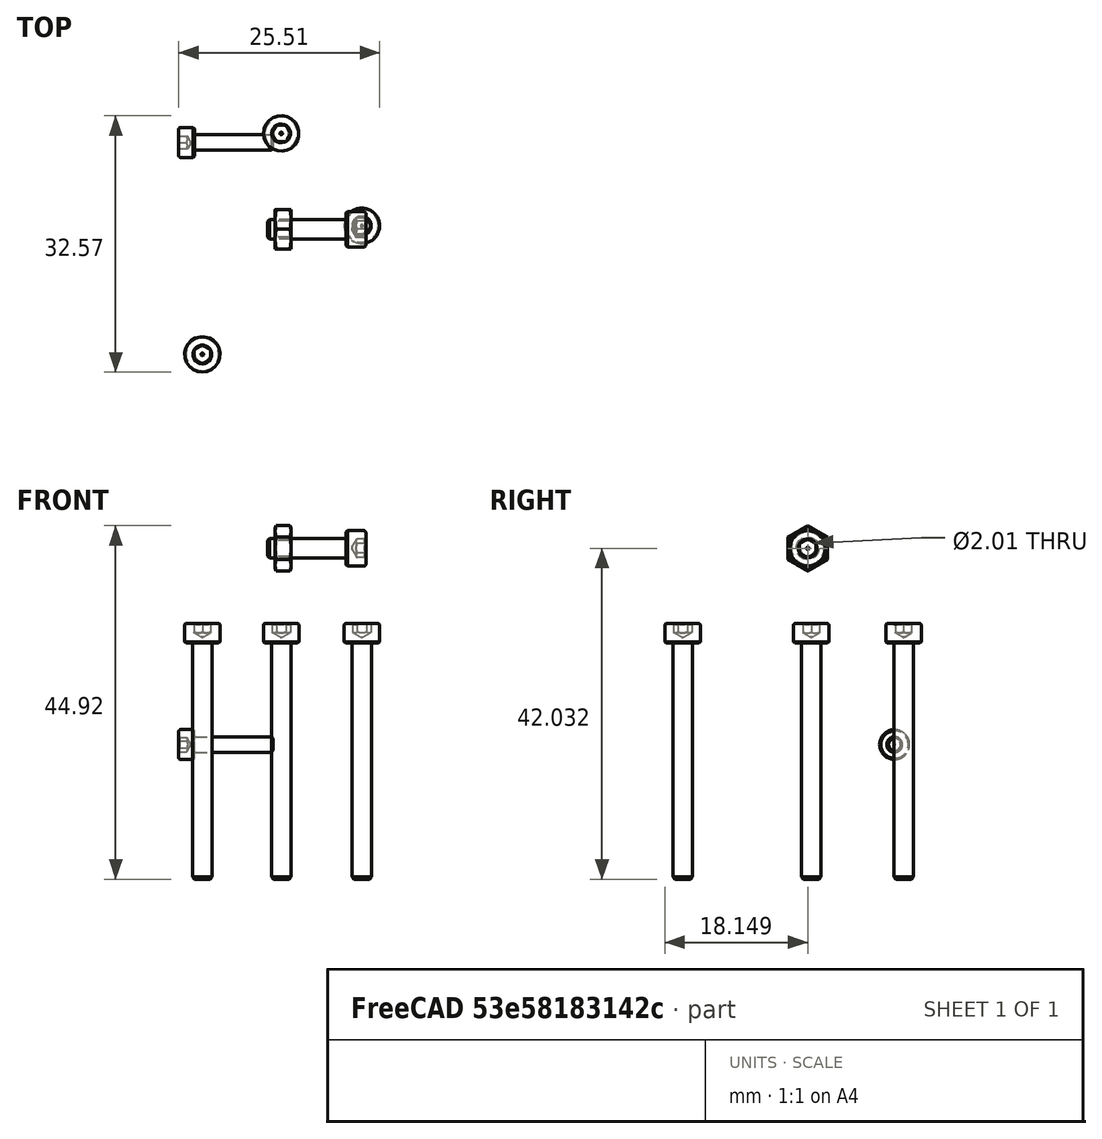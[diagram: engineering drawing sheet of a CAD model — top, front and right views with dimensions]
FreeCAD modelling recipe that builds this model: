
FCSTD DOCUMENT  (FreeCAD 0.19R24267 (Git))
Label: G5_extruder
License: All rights reserved
LicenseURL: http://en.wikipedia.org/wiki/All_rights_reserved
objects: Part::FeaturePython×6, App::Link×4, PartDesign::CoordinateSystem×2, App::DocumentObjectGroup×2, App::FeaturePython×1, App::Part×1
note: 8 computed .brp shape members not serialized (recipe doc carries the construction recipe); baked Part::Feature solids carry a one-line shape summary decoded from their .brp
EXTERNAL_REF file=G5_BASE.FCStd obj=LCS_1
EXTERNAL_REF file=G5_BASE.FCStd obj=Part
EXTERNAL_REF file=G5_BASE.FCStd obj=LCS_2
EXTERNAL_REF file=G5_TOP.FCStd obj=LCS_1
EXTERNAL_REF file=G5_TOP.FCStd obj=Part
EXTERNAL_REF file=G5_CAP.FCStd obj=LCS_1
EXTERNAL_REF file=G5_TOP.FCStd obj=LCS_2
EXTERNAL_REF file=G5_CAP.FCStd obj=Part
EXTERNAL_REF file=G5_BASE.FCStd obj=LCS_3
EXTERNAL_REF file=G5_TENSIONER.FCStd obj=LCS_1
EXTERNAL_REF file=G5_TENSIONER.FCStd obj=Part
EXTERNAL_REF file=G5_CAP.FCStd obj=LCS_4
EXTERNAL_REF file=G5_CAP.FCStd obj=LCS_3
EXTERNAL_REF file=G5_CAP.FCStd obj=LCS_2
EXTERNAL_REF file=G5_BASE.FCStd obj=LCS_4
EXTERNAL_REF file=G5_CAP.FCStd obj=LCS_5
EXTERNAL_REF file=G5_CAP.FCStd obj=LCS_6
EXTERNAL_REF file=G5_BASE.FCStd obj=LCS_5

FEATURE [PartDesign::CoordinateSystem] LCS_Origin
  AttacherType = Attacher::AttachEngine3D
  MapMode = 2
  Support = -> [X_Axis]
FEATURE [App::DocumentObjectGroup] Constraints
FEATURE [App::FeaturePython] Variables  # WARN: FeaturePython — macro-defined, semantics opaque (R4)
FEATURE [App::Link] G5_BASE_G5_BASE
  AssemblyType = Asm4EE
  AttachedBy = #LCS_1
  AttachedTo = Parent Assembly#LCS_Origin
  AttachmentOffset = pos=(0,0,0) rot=(0.707107,0.707107,0;3.14159rad)
  LinkPlacement = pos=(120,-8.89e-14,-0.0600001) rot=(0,0,1;0rad)
  LinkedObject = -> <external G5_BASE.FCStd>#Part
  Placement = pos=(120,-8.89e-14,-0.0600001) rot=(0,0,1;0rad)
  expr: Placement = LCS_Origin.Placement * AttachmentOffset * G5_BASE#LCS_1.Placement ^ -1
FEATURE [App::Link] G5_TOP_G5_TOP
  AssemblyType = Asm4EE
  AttachedBy = #LCS_1
  AttachedTo = G5_BASE_G5_BASE#LCS_2
  AttachmentOffset = pos=(0,0,0) rot=(0.707107,0.707107,0;3.14159rad)
  LinkPlacement = pos=(119.999,-2.82409e-05,-0.0599402) rot=(0,1,0;6.28318rad)
  LinkedObject = -> <external G5_TOP.FCStd>#Part
  Placement = pos=(119.999,-2.82409e-05,-0.0599402) rot=(0,1,0;6.28318rad)
  expr: Placement = G5_BASE_G5_BASE.Placement * G5_BASE#LCS_2.Placement * AttachmentOffset * G5_TOP#LCS_1.Placement ^ -1
FEATURE [App::Link] G5_CAP_G5_CAP
  AssemblyType = Asm4EE
  AttachedBy = #LCS_1
  AttachedTo = G5_TOP_G5_TOP#LCS_2
  AttachmentOffset = pos=(0,0,0) rot=(0,0,1;1.5708rad)
  LinkPlacement = pos=(120.005,-0.0748696,-0.0599954) rot=(-0.00069,-6.9e-05,1;6.28276rad)
  LinkedObject = -> <external G5_CAP.FCStd>#Part
  Placement = pos=(120.005,-0.0748696,-0.0599954) rot=(-0.00069,-6.9e-05,1;6.28276rad)
  expr: Placement = G5_TOP_G5_TOP.Placement * G5_TOP#LCS_2.Placement * AttachmentOffset * G5_CAP#LCS_1.Placement ^ -1
FEATURE [App::Link] G5_TENSIONER_G5_TENSIONER
  AssemblyType = Asm4EE
  AttachedBy = #LCS_1
  AttachedTo = G5_BASE_G5_BASE#LCS_3
  AttachmentOffset = pos=(0,0,0) rot=(-0.707107,-0.707107,0;3.14159rad)
  LinkPlacement = pos=(12.06,-34.3342,61.6058) rot=(0.57735,0.57735,-0.57735;4.18879rad)
  LinkedObject = -> <external G5_TENSIONER.FCStd>#Part
  Placement = pos=(12.06,-34.3342,61.6058) rot=(0.57735,0.57735,-0.57735;4.18879rad)
  expr: Placement = G5_BASE_G5_BASE.Placement * G5_BASE#LCS_3.Placement * AttachmentOffset * G5_TENSIONER#LCS_1.Placement ^ -1
FEATURE [Part::FeaturePython] Screw001  label="M2.5x30-Screw041"  # Fasteners workbench fastener (typed FeaturePython)
  AssemblyType = Asm4EE
  AttachedBy = Origin
  AttachedTo = G5_CAP_G5_CAP#LCS_4
  AttachmentOffset = pos=(0,0,0) rot=(0,-1,0;3.14159rad)
  Placement = pos=(5.25469,13.8071,25.84) rot=(0,0,1;3.14117rad)
  diameter = 3
  invert = false
  length = 10
  lengthCustom = 30
  matchOuter = false
  offset = 0
  thread = false
  type = 32
  expr: Placement = G5_CAP_G5_CAP.Placement * G5_CAP#LCS_4.Placement * AttachmentOffset
FEATURE [Part::FeaturePython] Screw002  label="M2.5x30-Screw042"  # Fasteners workbench fastener (typed FeaturePython)
  AssemblyType = Asm4EE
  AttachedBy = Origin
  AttachedTo = G5_CAP_G5_CAP#LCS_3
  AttachmentOffset = pos=(0,0,0) rot=(0,0,1;3.14159rad)
  Placement = pos=(-4.75709,-14.2647,25.84) rot=(0,0,-1;1.57122rad)
  diameter = 3
  invert = false
  length = 10
  lengthCustom = 30
  matchOuter = false
  offset = 0
  thread = false
  type = 32
  expr: Placement = G5_CAP_G5_CAP.Placement * G5_CAP#LCS_3.Placement * AttachmentOffset
FEATURE [Part::FeaturePython] Screw003  label="M2.5x30-Screw"  # Fasteners workbench fastener (typed FeaturePython)
  AssemblyType = Asm4EE
  AttachedBy = Origin
  AttachedTo = G5_CAP_G5_CAP#LCS_2
  AttachmentOffset = pos=(0,0,0) rot=(0,0,1;3.14159rad)
  Placement = pos=(15.5062,2.07386,25.84) rot=(0,0,-1;3.14159rad)
  diameter = 3
  invert = false
  length = 10
  lengthCustom = 30
  matchOuter = false
  offset = 0
  thread = false
  type = 32
  expr: Placement = G5_CAP_G5_CAP.Placement * G5_CAP#LCS_2.Placement * AttachmentOffset
FEATURE [Part::FeaturePython] Screw004  label="M2x10-Screw"  # Fasteners workbench fastener (typed FeaturePython)
  AssemblyType = Asm4EE
  AttachedBy = Origin
  AttachedTo = G5_BASE_G5_BASE#LCS_4
  Placement = pos=(-5.75,12.6658,12.94) rot=(0.707107,0,-0.707107;3.14159rad)
  diameter = 2
  invert = false
  length = 5
  lengthCustom = 10
  matchOuter = false
  offset = 0
  thread = false
  type = 32
  expr: Placement = G5_BASE_G5_BASE.Placement * G5_BASE#LCS_4.Placement * AttachmentOffset
FEATURE [Part::FeaturePython] Screw005  label="M2.5x10-Screw"  # Fasteners workbench fastener (typed FeaturePython)
  AssemblyType = Asm4EE
  AttachedBy = Origin
  AttachedTo = G5_CAP_G5_CAP#LCS_5
  AttachmentOffset = pos=(0,0,0) rot=(0,1,0;3.14159rad)
  Placement = pos=(13.505,1.63524,37.8722) rot=(-0.000211,-1,0.000211;4.71239rad)
  diameter = 3
  invert = false
  length = 4
  lengthCustom = 10
  matchOuter = false
  offset = 0
  thread = false
  type = 32
  expr: Placement = G5_CAP_G5_CAP.Placement * G5_CAP#LCS_5.Placement * AttachmentOffset
FEATURE [Part::FeaturePython] Nut  label="M2.5-Nut"  # Fasteners workbench fastener (typed FeaturePython)
  AssemblyType = Asm4EE
  AttachedBy = Origin
  AttachedTo = G5_CAP_G5_CAP#LCS_6
  Placement = pos=(6.49955,1.6382,37.8722) rot=(0.000211,1,0.000211;4.71239rad)
  diameter = 3
  invert = false
  matchOuter = false
  offset = 0
  thread = false
  type = 7
  expr: Placement = G5_CAP_G5_CAP.Placement * G5_CAP#LCS_6.Placement * AttachmentOffset
FEATURE [App::DocumentObjectGroup] Group  label="Fasteners"
  Group = -> [Screw004,Screw003,Screw002,Screw001,Screw005,Nut]
FEATURE [PartDesign::CoordinateSystem] LCS_5
  AttacherType = Attacher::AttachEngine3D
  Placement = pos=(15.5062,2.07386,-3.88e-14) rot=(1,0,0;3.14159rad)
  expr: Placement = G5_BASE_G5_BASE.Placement * G5_BASE#LCS_5.Placement * AttachmentOffset
FEATURE [App::Part] Model
  Configuration = 0
  Group = -> [LCS_Origin,Constraints,Variables,G5_BASE_G5_BASE,G5_TOP_G5_TOP,G5_CAP_G5_CAP,G5_TENSIONER_G5_TENSIONER,Screw003,Screw004,Screw001,Screw002,Group,Screw005,Nut,LCS_5]
  Origin = -> Origin
  Type = Assembly4 Model
